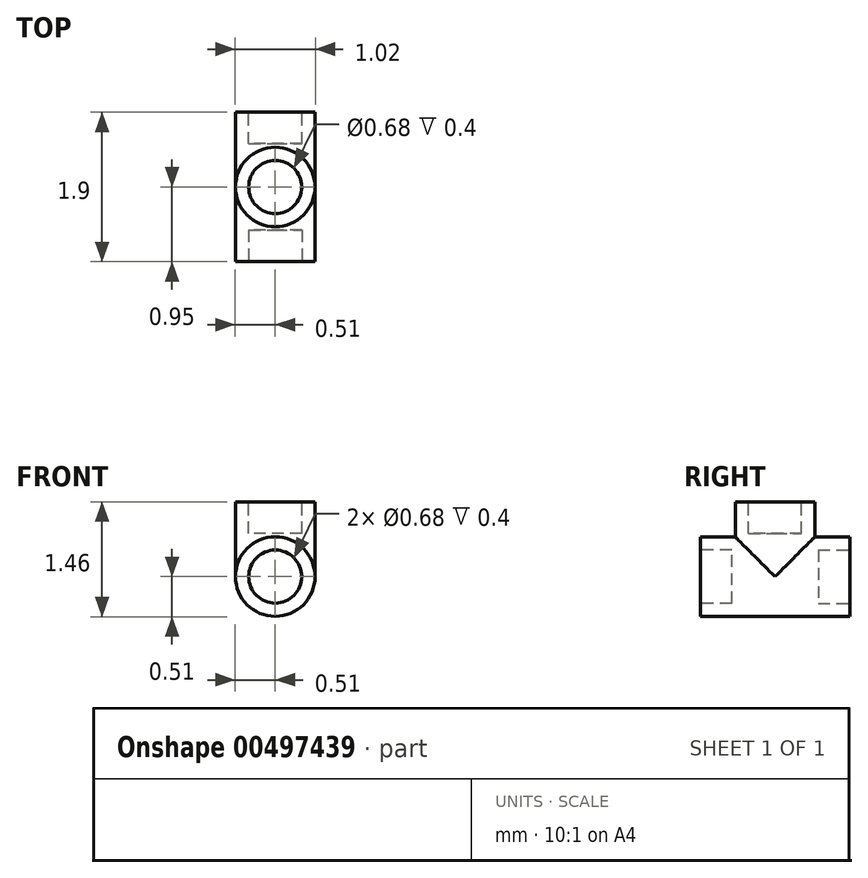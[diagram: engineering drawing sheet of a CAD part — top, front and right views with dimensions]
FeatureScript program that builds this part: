
annotation { "Feature Type Name" : "Feature", "Feature Type Description" : "" }
export const myFeature = defineFeature(function(context is Context, id is Id, definition is map)
    precondition{}
    {
        {
            var Q0;
            Q0=qCreatedBy(makeId("Front.planeOp"),FACE);
            var sketch = newSketch(context, id + "F0", { "sketchPlane" : qUnion([Q0])});
            skCircle(sketch, "E0", {"center": v(0, 0) * mm, "radius": 0.5 * mm});
            skSolve(sketch);
        }
        {
            var Q0;
            Q0 = qSketchRegion(id + "F0", true);
            extrude(context, id + "F1", {"entities" : qUnion([Q0]), "depth" : 1.9 * mm});
        }
        {
            var Q0;
            Q0=qCreatedBy(makeId("Top.planeOp"),FACE);
            var sketch = newSketch(context, id + "F2", { "sketchPlane" : qUnion([Q0])});
            skLineSegment(sketch, "E1", {"start": v(0, 0) * mm, "end": v(0, -0.95) * mm});
            skCircle(sketch, "E2", {"center": v(0, -0.95) * mm, "radius": 0.5 * mm});
            skSolve(sketch);
        }
        {
            var Q0;
            Q0 = qSketchRegion(id + "F2", true);
            extrude(context, id + "F3", {"entities" : qUnion([Q0]), "operationType" : NewBodyOperationType.ADD, "depth" : .95 * mm});
        }
        {
            var Q0;
            Q0=makeQuery(id+"F1.opExtrude","CAP_FACE",FACE,{"disambiguationData":[OSD([sQuery(id+"F0.wireOp",EDGE,"E0")])],"isStart":true});
            var sketch = newSketch(context, id + "F4", { "sketchPlane" : qUnion([Q0])});
            skCircle(sketch, "E3", {"center": v(0, 0) * mm, "radius": 0.34 * mm});
            skSolve(sketch);
        }
        {
            var Q0;
            Q0 = qSketchRegion(id + "F4", true);
            extrude(context, id + "F5", {"entities" : qUnion([Q0]), "operationType" : NewBodyOperationType.REMOVE, "oppositeDirection" : true, "depth" : .4 * mm});
        }
        {
            var Q0;
            Q0=makeQuery(id+"F3.opExtrude","CAP_FACE",FACE,{"disambiguationData":[OSD([sQuery(id+"F2.wireOp",EDGE,"E2")])],"isStart":false});
            var sketch = newSketch(context, id + "F6", { "sketchPlane" : qUnion([Q0])});
            skCircle(sketch, "E4", {"center": v(0, -0.95) * mm, "radius": 0.34 * mm});
            skSolve(sketch);
        }
        {
            var Q0;
            Q0 = qSketchRegion(id + "F6", true);
            extrude(context, id + "F7", {"entities" : qUnion([Q0]), "operationType" : NewBodyOperationType.REMOVE, "oppositeDirection" : true, "depth" : .4 * mm});
        }
        {
            var Q0;
            Q0=makeQuery(id+"F1.opExtrude","CAP_FACE",FACE,{"disambiguationData":[OSD([sQuery(id+"F0.wireOp",EDGE,"E0")])],"isStart":false});
            var sketch = newSketch(context, id + "F8", { "sketchPlane" : qUnion([Q0])});
            skCircle(sketch, "E5", {"center": v(0, 0) * mm, "radius": 0.34 * mm});
            skSolve(sketch);
        }
        {
            var Q0;
            Q0 = qSketchRegion(id + "F8", true);
            extrude(context, id + "F9", {"entities" : qUnion([Q0]), "operationType" : NewBodyOperationType.REMOVE, "oppositeDirection" : true, "depth" : .4 * mm});
        }
    });
